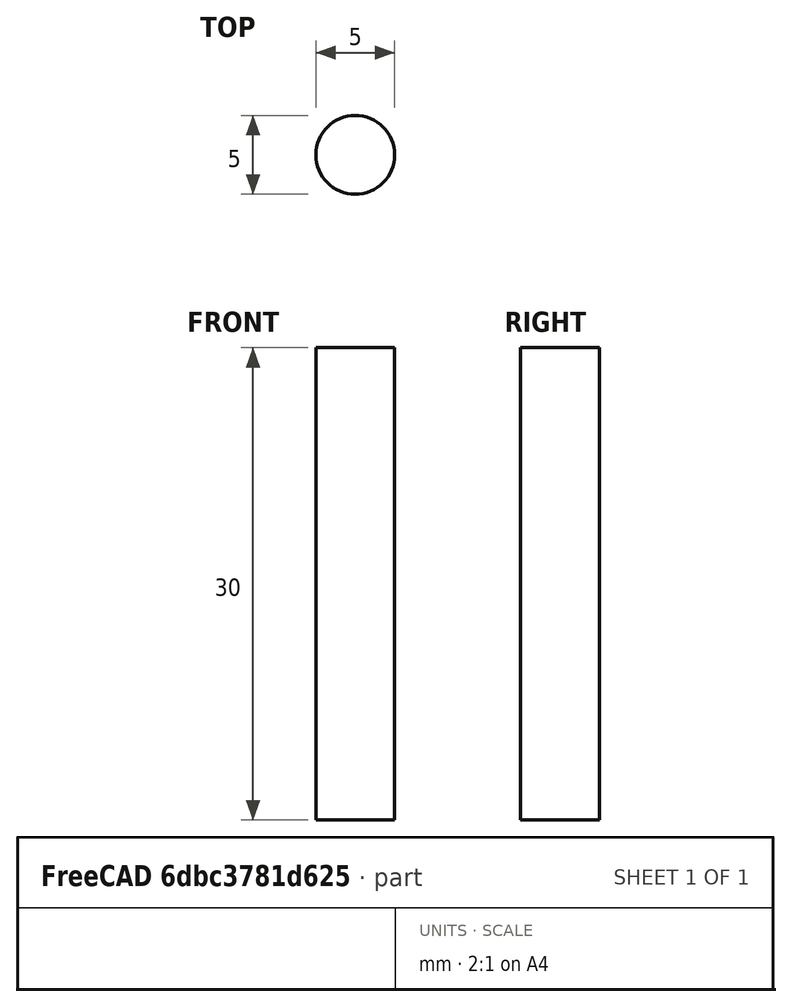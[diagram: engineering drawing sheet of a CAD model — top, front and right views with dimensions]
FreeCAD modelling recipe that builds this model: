
FCSTD DOCUMENT  (FreeCAD 0.20R29603 (Git))
Label: cylinder_v2
License: All rights reserved
LicenseURL: http://en.wikipedia.org/wiki/All_rights_reserved
objects: TechDraw::DrawProjGroupItem×2, TechDraw::DrawViewDimension×2, Part::Cylinder×1, TechDraw::DrawSVGTemplate×1, TechDraw::DrawProjGroup×1, TechDraw::DrawPage×1
note: 1 computed .brp shape members not serialized (recipe doc carries the construction recipe); baked Part::Feature solids carry a one-line shape summary decoded from their .brp

FEATURE [Part::Cylinder] Cylinder  label="cylinder"
  Angle = 360
  AttacherType = Attacher::AttachEngine3D
  FirstAngle = 0
  Height = 30
  Radius = 2.5
  SecondAngle = 0
FEATURE [TechDraw::DrawSVGTemplate] Template
  EditableTexts = Designed_by_Name=Белкин Никита; FC-Date=20.04.2023; FC-SC=4:1; FC-Title=Соединение для шарнира
  Height = 210
  Orientation = 1
  Width = 297
FEATURE [TechDraw::DrawProjGroupItem] ProjItem  label="Front"
  CoarseView = false
  Direction = (0,0,1)
  Focus = 100
  HardHidden = false
  IsoCount = 0
  IsoHidden = false
  IsoVisible = false
  LockPosition = true
  Perspective = false
  Rotation = 0
  RotationVector = (1,0,0)
  Scale = 4
  ScaleType = 2
  SeamHidden = false
  SeamVisible = true
  SmoothHidden = false
  SmoothVisible = true
  Source = -> [Cylinder]
  Type = 0
  X = 0
  XDirection = (1,0,0)
  Y = 0
FEATURE [TechDraw::DrawProjGroupItem] ProjItem001  label="Left"
  CoarseView = false
  Direction = (-1,0,1e-16)
  Focus = 100
  HardHidden = false
  IsoCount = 0
  IsoHidden = false
  IsoVisible = false
  LockPosition = false
  Perspective = false
  Rotation = 0
  RotationVector = (1,0,0)
  ScaleType = 2
  SeamHidden = false
  SeamVisible = true
  SmoothHidden = false
  SmoothVisible = true
  Source = -> [Cylinder]
  Type = 1
  X = 135
  XDirection = (1e-16,0,1)
  Y = 0
FEATURE [TechDraw::DrawProjGroup] ProjGroup
  Anchor = -> ProjItem
  AutoDistribute = true
  LockPosition = false
  ProjectionType = 0
  Rotation = 0
  Scale = 4
  ScaleType = 2
  Source = -> [Cylinder]
  Views = -> [ProjItem,ProjItem001]
  X = 74.2554
  Y = 116.263
  spacingX = 15
  spacingY = 15
FEATURE [TechDraw::DrawViewDimension] Dimension
  AngleOverride = false
  Arbitrary = false
  ArbitraryTolerances = false
  EqualTolerance = true
  ExtensionAngle = 0
  FormatSpec = ⌀%.2w
  FormatSpecOverTolerance = %+.2w
  FormatSpecUnderTolerance = %+.2w
  Inverted = false
  LineAngle = 0
  LockPosition = false
  MeasureType = 1
  OverTolerance = 0
  References2D = -> [ProjItem]
  Rotation = 0
  ScaleType = 0
  TheoreticalExact = false
  Type = 5
  UnderTolerance = 0
  X = 9.6541
  Y = 23.2158
FEATURE [TechDraw::DrawViewDimension] Dimension001
  AngleOverride = false
  Arbitrary = false
  ArbitraryTolerances = false
  EqualTolerance = true
  ExtensionAngle = 0
  FormatSpec = %.2w
  FormatSpecOverTolerance = %+.2w
  FormatSpecUnderTolerance = %+.2w
  Inverted = false
  LineAngle = 0
  LockPosition = false
  MeasureType = 1
  OverTolerance = 0
  References2D = -> [ProjItem001]
  Rotation = 0
  ScaleType = 0
  TheoreticalExact = false
  Type = 1
  UnderTolerance = 0
  X = -1.37916
  Y = -11.8673
FEATURE [TechDraw::DrawPage] Page
  KeepUpdated = true
  NextBalloonIndex = 1
  ProjectionType = 0
  Template = -> Template
  Views = -> [ProjGroup,Dimension,Dimension001]
